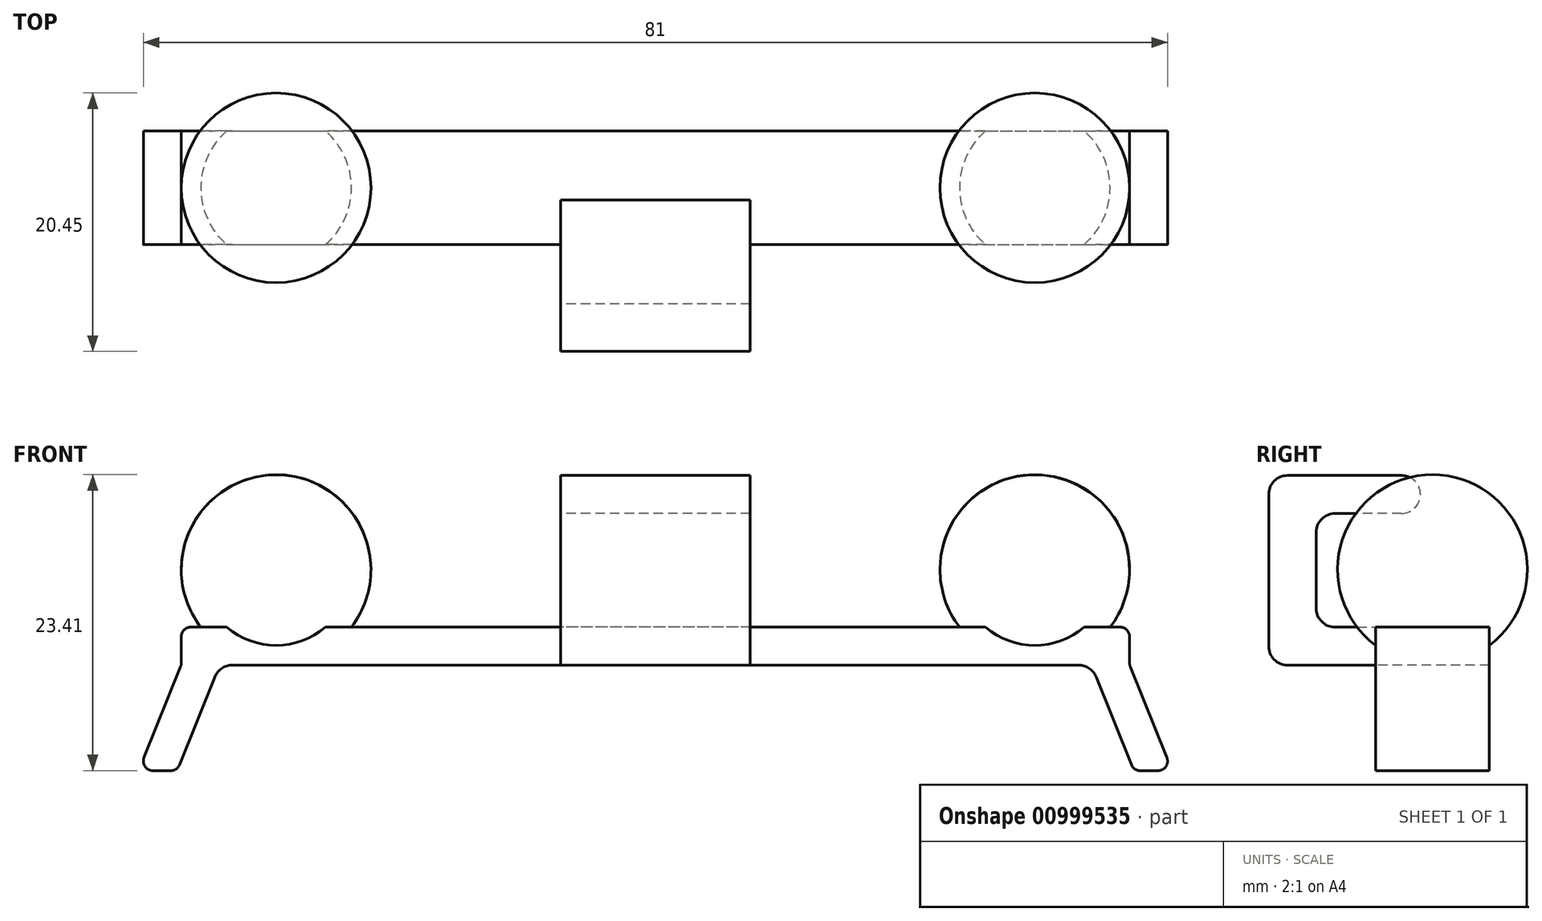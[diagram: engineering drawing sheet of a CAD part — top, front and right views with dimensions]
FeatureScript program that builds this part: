
annotation { "Feature Type Name" : "Feature", "Feature Type Description" : "" }
export const myFeature = defineFeature(function(context is Context, id is Id, definition is map)
    precondition{}
    {
        {
            var Q0;
            Q0=qCreatedBy(makeId("Front.planeOp"),FACE);
            var sketch = newSketch(context, id + "F0", { "sketchPlane" : qUnion([Q0])});
            skLineSegment(sketch, "E0", {"start": v(-22.3, 0) * mm, "end": v(0, 0) * mm});
            skArc(sketch, "E1", {"start": v(-15, 5.08) * mm, "mid": v(-20.04, 10.04) * mm, "end": v(-25, 5) * mm});
            skLineSegment(sketch, "E2", {"start": v(-25, 5) * mm, "end": v(-15, 5.08) * mm});
            skLineSegment(sketch, "E3", {"start": v(0, 0) * mm, "end": v(0, 2) * mm});
            skLineSegment(sketch, "E4", {"start": v(0, 2) * mm, "end": v(-24.5, 2) * mm});
            skLineSegment(sketch, "E5", {"start": v(-25, 1.5) * mm, "end": v(-25, 0.1) * mm});
            skLineSegment(sketch, "E6", {"start": v(-25, 2) * mm, "end": v(-25, 5) * mm, "construction": true});
            skLineSegment(sketch, "E7", {"start": v(-25.04, -0.09) * mm, "end": v(-26.96, -4.88) * mm});
            skLineSegment(sketch, "E8", {"start": v(-26.5, -5.57) * mm, "end": v(-25.55, -5.57) * mm});
            skLineSegment(sketch, "E9", {"start": v(-25.1, -5.25) * mm, "end": v(-23.23, -0.63) * mm});
            skPoint(sketch, "E10.visualSharp", {"position": v(-22.98, 0) * mm});
            skArc(sketch, "E10.filletArc", {"start": v(-22.3, 0) * mm, "mid": v(-22.86, -0.17) * mm, "end": v(-23.23, -0.63) * mm});
            skPoint(sketch, "E11.visualSharp", {"position": v(-27.24, -5.57) * mm});
            skArc(sketch, "E11.filletArc", {"start": v(-26.96, -4.88) * mm, "mid": v(-26.91, -5.35) * mm, "end": v(-26.5, -5.57) * mm});
            skPoint(sketch, "E12.visualSharp", {"position": v(-25.22, -5.57) * mm});
            skArc(sketch, "E12.filletArc", {"start": v(-25.55, -5.57) * mm, "mid": v(-25.27, -5.48) * mm, "end": v(-25.1, -5.25) * mm});
            skPoint(sketch, "E13.visualSharp", {"position": v(-25, 0) * mm});
            skArc(sketch, "E13.filletArc", {"start": v(-25.04, -0.09) * mm, "mid": v(-25, 0) * mm, "end": v(-25, 0.1) * mm});
            skPoint(sketch, "E14.visualSharp", {"position": v(-25, 2) * mm});
            skArc(sketch, "E14.filletArc", {"start": v(-24.5, 2) * mm, "mid": v(-24.85, 1.85) * mm, "end": v(-25, 1.5) * mm});
            skSolve(sketch);
        }
        {
            var Q0;
            Q0=qCreatedBy(makeId("Right.planeOp"),FACE);
            var sketch = newSketch(context, id + "F1", { "sketchPlane" : qUnion([Q0])});
            skLineSegment(sketch, "E15", {"start": v(0, 0) * mm, "end": v(-7.63, 0) * mm});
            skLineSegment(sketch, "E16", {"start": v(-8.63, 1) * mm, "end": v(-8.63, 9) * mm});
            skLineSegment(sketch, "E17", {"start": v(-7.63, 10) * mm, "end": v(-1.63, 10) * mm});
            skLineSegment(sketch, "E18", {"start": v(-0.63, 9) * mm, "end": v(-0.63, 9) * mm});
            skLineSegment(sketch, "E19", {"start": v(-1.63, 8) * mm, "end": v(-5.13, 8) * mm});
            skLineSegment(sketch, "E20", {"start": v(-6.13, 7) * mm, "end": v(-6.13, 3) * mm});
            skLineSegment(sketch, "E21", {"start": v(-5.13, 2) * mm, "end": v(0, 2) * mm});
            skLineSegment(sketch, "E22", {"start": v(0, 2) * mm, "end": v(0, 0) * mm});
            skPoint(sketch, "E23.visualSharp", {"position": v(-0.63, 8) * mm});
            skArc(sketch, "E23.filletArc", {"start": v(-1.63, 8) * mm, "mid": v(-0.93, 8.3) * mm, "end": v(-0.63, 9) * mm});
            skPoint(sketch, "E24.visualSharp", {"position": v(-0.63, 10) * mm});
            skArc(sketch, "E24.filletArc", {"start": v(-0.63, 9) * mm, "mid": v(-0.93, 9.7) * mm, "end": v(-1.63, 10) * mm});
            skPoint(sketch, "E25.visualSharp", {"position": v(-8.63, 10) * mm});
            skArc(sketch, "E25.filletArc", {"start": v(-7.63, 10) * mm, "mid": v(-8.34, 9.7) * mm, "end": v(-8.63, 9) * mm});
            skPoint(sketch, "E26.visualSharp", {"position": v(-6.13, 8) * mm});
            skArc(sketch, "E26.filletArc", {"start": v(-5.13, 8) * mm, "mid": v(-5.84, 7.7) * mm, "end": v(-6.13, 7) * mm});
            skPoint(sketch, "E27.visualSharp", {"position": v(-6.13, 2) * mm});
            skArc(sketch, "E27.filletArc", {"start": v(-6.13, 3) * mm, "mid": v(-5.84, 2.3) * mm, "end": v(-5.13, 2) * mm});
            skPoint(sketch, "E28.visualSharp", {"position": v(-8.63, 0) * mm});
            skArc(sketch, "E28.filletArc", {"start": v(-8.63, 1) * mm, "mid": v(-8.34, 0.3) * mm, "end": v(-7.63, 0) * mm});
            skSolve(sketch);
        }
        {
            var Q0;
            Q0=makeQuery(id+"F0.imprint","IMPRINT",FACE,{"disambiguationData":[TD([[makeQuery(id+"F0.imprint","IMPRINT",EDGE,{"derivedFrom":sQuery(id+"F0.wireOp",EDGE,"E1")}),1.0]])]});
            var Q1;
            Q1=sQuery(id+"F0.wireOp",EDGE,"E2");
            revolve(context, id + "F2", {"surfaceOperationType" : NewSurfaceOperationType.NEW, "entities" : qUnion([Q0]), "axis" : qUnion([Q1]), "revolveType" : RevolveType.FULL});
        }
        {
            var Q0;
            {var subQ0=sQuery(id+"F0.wireOp",EDGE,"E7");Q0=makeQuery(id+"F0.imprint","IMPRINT",FACE,{"disambiguationData":[TD([[makeQuery(id+"F0.imprint","IMPRINT",EDGE,{"derivedFrom":subQ0}),1.0]])]});}
            var Q1;
            {var subQ0=sQuery(id+"F0.wireOp",EDGE,"E3");Q1=makeQuery(id+"F0.imprint","IMPRINT",FACE,{"disambiguationData":[TD([[makeQuery(id+"F0.imprint","IMPRINT",EDGE,{"derivedFrom":subQ0}),1.0]])]});}
            extrude(context, id + "F3", {"entities" : qUnion([Q0, Q1]), "oppositeDirection" : true, "depth" : 3 * mm, "offsetDistance" : 25.4 * mm, "hasSecondDirection" : true, "secondDirectionOppositeDirection" : false, "secondDirectionDepth" : 3 * mm});
        }
        {
            var Q0;
            Q0=makeQuery(id+"F2.opRevolve","SWEPT_BODY",BODY,{"disambiguationData":[OSD([sQuery(id+"F0.wireOp",EDGE,"E1"),sQuery(id+"F0.wireOp",EDGE,"E2")])]});
            var Q1;
            Q1=makeQuery(id+"F3.opExtrude","SWEPT_BODY",BODY,{"disambiguationData":[OSD([sQuery(id+"F0.wireOp",EDGE,"E0"),sQuery(id+"F0.wireOp",EDGE,"E3"),sQuery(id+"F0.wireOp",EDGE,"E4"),sQuery(id+"F0.wireOp",EDGE,"E5"),sQuery(id+"F0.wireOp",EDGE,"E7"),sQuery(id+"F0.wireOp",EDGE,"E8"),sQuery(id+"F0.wireOp",EDGE,"E9")])]});
            var Q2;
            Q2=qCreatedBy(makeId("Right.planeOp"),FACE);
            mirror(context, id + "F4", {"operationType" : NewBodyOperationType.ADD, "entities" : qUnion([Q0, Q1]), "mirrorPlane" : qUnion([Q2])});
        }
        {
            var Q0;
            Q0=makeQuery(id+"F1.imprint","IMPRINT",FACE,{"disambiguationData":[TD([[makeQuery(id+"F1.imprint","IMPRINT",EDGE,{"derivedFrom":sQuery(id+"F1.wireOp",EDGE,"E15")}),-1.0]])]});
            extrude(context, id + "F5", {"entities" : qUnion([Q0]), "operationType" : NewBodyOperationType.ADD, "depth" : 5 * mm, "offsetDistance" : 25 * mm, "hasSecondDirection" : true, "secondDirectionOppositeDirection" : true, "secondDirectionDepth" : 5 * mm});
        }
        {
            var Q0;
            Q0=makeQuery(id+"F2.opRevolve","SWEPT_BODY",BODY,{"disambiguationData":[OSD([sQuery(id+"F0.wireOp",EDGE,"E1"),sQuery(id+"F0.wireOp",EDGE,"E2")])]});
            var Q1;
            Q1=makeQuery(id+"F5.opExtrude","CAP_VERTEX",VERTEX,{"disambiguationData":[OSD([sQuery(id+"F1.wireOp",EDGE,"E17"),sQuery(id+"F1.wireOp",EDGE,"E24.filletArc")])],"isStart":false});
            transform(context, id + "F6", {"entities" : qUnion([Q0]), "transformType" : TransformType.SCALE_UNIFORMLY, "scale" : 1.5, "scalePoint" : qUnion([Q1]), "makeCopy" : false});
        }
    });
